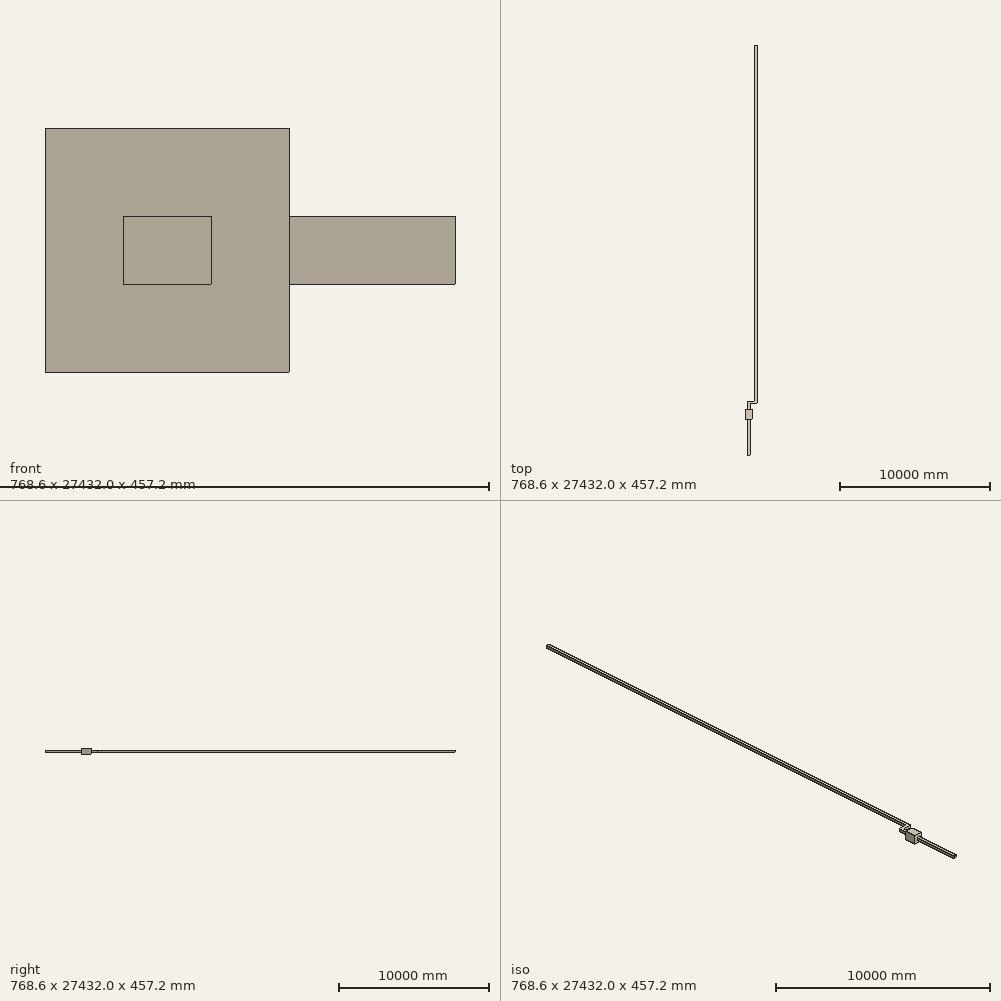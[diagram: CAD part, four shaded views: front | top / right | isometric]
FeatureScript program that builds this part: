
annotation { "Feature Type Name" : "Feature", "Feature Type Description" : "" }
export const myFeature = defineFeature(function(context is Context, id is Id, definition is map)
    precondition{}
    {
        {
            var Q0;
            Q0=qCreatedBy(makeId("Front.planeOp"),FACE);
            var sketch = newSketch(context, id + "F0", { "sketchPlane" : qUnion([Q0])});
            skLineSegment(sketch, "E0.bottom", {"start": v(0, 0) * mm, "end": v(165.6, 0) * mm});
            skLineSegment(sketch, "E0.top", {"start": v(0, 127) * mm, "end": v(165.6, 127) * mm});
            skLineSegment(sketch, "E0.left", {"start": v(0, 0) * mm, "end": v(0, 127) * mm});
            skLineSegment(sketch, "E0.right", {"start": v(165.6, 0) * mm, "end": v(165.6, 127) * mm});
            skSolve(sketch);
        }
        {
            var Q0;
            Q0=makeQuery(id+"F0.imprint","IMPRINT",FACE,{"disambiguationData":[TD([[makeQuery(id+"F0.imprint","IMPRINT",EDGE,{"derivedFrom":sQuery(id+"F0.wireOp",EDGE,"E0.bottom")}),1.0]])]});
            extrude(context, id + "F1", {"entities" : qUnion([Q0]), "oppositeDirection" : true, "depth" : 2438.4 * mm, "offsetDistance" : 25.4 * mm});
        }
        {
            var Q0;
            Q0=makeQuery(id+"F1.opExtrude","CAP_FACE",FACE,{"disambiguationData":[OSD([sQuery(id+"F0.wireOp",EDGE,"E0.bottom"),sQuery(id+"F0.wireOp",EDGE,"E0.top"),sQuery(id+"F0.wireOp",EDGE,"E0.left"),sQuery(id+"F0.wireOp",EDGE,"E0.right")])],"isStart":false});
            var sketch = newSketch(context, id + "F2", { "sketchPlane" : qUnion([Q0])});
            skLineSegment(sketch, "E1.bottom", {"start": v(145.8, -165.1) * mm, "end": v(-311.4, -165.1) * mm});
            skLineSegment(sketch, "E1.top", {"start": v(145.8, 292.1) * mm, "end": v(-311.4, 292.1) * mm});
            skLineSegment(sketch, "E1.left", {"start": v(145.8, -165.1) * mm, "end": v(145.8, 292.1) * mm});
            skLineSegment(sketch, "E1.right", {"start": v(-311.4, -165.1) * mm, "end": v(-311.4, 292.1) * mm});
            skPoint(sketch, "E1.middle", {"position": v(-82.8, 63.5) * mm});
            skPoint(sketch, "E1.middle.positionSnap0", {"position": v(-82.8, 127) * mm});
            skPoint(sketch, "E1.middle.positionSnap1", {"position": v(0, 63.5) * mm});
            skPoint(sketch, "E1.centerSnap0", {"position": v(-82.8, 127) * mm});
            skPoint(sketch, "E1.centerSnap1", {"position": v(0, 63.5) * mm});
            skSolve(sketch);
        }
        {
            var Q0;
            Q0=makeQuery(id+"F2.imprint","IMPRINT",FACE,{"disambiguationData":[TD([[makeQuery(id+"F2.imprint","IMPRINT",EDGE,{"derivedFrom":makeQuery(id+"F1.opExtrude","CAP_EDGE",EDGE,{"disambiguationData":[OSD([sQuery(id+"F0.wireOp",EDGE,"E0.bottom")])],"isStart":false})}),-1.0]])]});
            var Q1;
            Q1=makeQuery(id+"F2.imprint","IMPRINT",FACE,{"disambiguationData":[TD([[makeQuery(id+"F2.imprint","IMPRINT",EDGE,{"derivedFrom":sQuery(id+"F2.wireOp",EDGE,"E1.bottom")}),-1.0]])]});
            extrude(context, id + "F3", {"entities" : qUnion([Q0, Q1]), "depth" : 609.6 * mm, "offsetDistance" : 25.4 * mm});
        }
        {
            var Q0;
            Q0=makeQuery(id+"F3.opExtrude","CAP_FACE",FACE,{"disambiguationData":[OSD([sQuery(id+"F2.wireOp",EDGE,"E1.bottom"),sQuery(id+"F2.wireOp",EDGE,"E1.top"),sQuery(id+"F2.wireOp",EDGE,"E1.left"),sQuery(id+"F2.wireOp",EDGE,"E1.right")])],"isStart":false});
            var sketch = newSketch(context, id + "F4", { "sketchPlane" : qUnion([Q0])});
            skLineSegment(sketch, "E2.bottom", {"start": v(0, 0) * mm, "end": v(-165.6, 0) * mm});
            skLineSegment(sketch, "E2.top", {"start": v(0, 127) * mm, "end": v(-165.6, 127) * mm});
            skLineSegment(sketch, "E2.left", {"start": v(0, 0) * mm, "end": v(0, 127) * mm});
            skLineSegment(sketch, "E2.right", {"start": v(-165.6, 0) * mm, "end": v(-165.6, 127) * mm});
            skPoint(sketch, "E2.middle", {"position": v(-82.8, 63.5) * mm});
            skPoint(sketch, "E2.middle.positionSnap0", {"position": v(145.8, 63.5) * mm});
            skPoint(sketch, "E2.middle.positionSnap1", {"position": v(-82.8, 292.1) * mm});
            skPoint(sketch, "E2.centerSnap0", {"position": v(145.8, 63.5) * mm});
            skPoint(sketch, "E2.centerSnap1", {"position": v(-82.8, 292.1) * mm});
            skSolve(sketch);
        }
        {
            var Q0;
            Q0=makeQuery(id+"F4.imprint","IMPRINT",FACE,{"disambiguationData":[TD([[makeQuery(id+"F4.imprint","IMPRINT",EDGE,{"derivedFrom":sQuery(id+"F4.wireOp",EDGE,"E2.bottom")}),-1.0]])]});
            extrude(context, id + "F5", {"entities" : qUnion([Q0]), "depth" : 203.2 * mm, "offsetDistance" : 25.4 * mm});
        }
        {
            var Q0;
            Q0=makeQuery(id+"F5.opExtrude","CAP_FACE",FACE,{"disambiguationData":[OSD([sQuery(id+"F4.wireOp",EDGE,"E2.bottom"),sQuery(id+"F4.wireOp",EDGE,"E2.top"),sQuery(id+"F4.wireOp",EDGE,"E2.left"),sQuery(id+"F4.wireOp",EDGE,"E2.right")])],"isStart":false});
            extrude(context, id + "F6", {"entities" : qUnion([Q0]), "operationType" : NewBodyOperationType.ADD, "depth" : 387.6 * mm, "offsetDistance" : 25.4 * mm});
        }
        {
            var Q0;
            {var subQ0=sQuery(id+"F4.wireOp",EDGE,"E2.right");Q0=makeQuery(id+"F6.boolean.opBoolean","MERGE",FACE,{"derivedFrom":[makeQuery(id+"F5.opExtrude","SWEPT_FACE",FACE,{"disambiguationData":[OSD([subQ0])]}),makeQuery(id+"F6.opExtrude","SWEPT_FACE",FACE,{"disambiguationData":[OSD([subQ0])]})]});}
            var sketch = newSketch(context, id + "F7", { "sketchPlane" : qUnion([Q0])});
            skLineSegment(sketch, "E3.bottom", {"start": v(3638.8, 127) * mm, "end": v(3473.2, 127) * mm});
            skLineSegment(sketch, "E3.top", {"start": v(3638.8, 0) * mm, "end": v(3473.2, 0) * mm});
            skLineSegment(sketch, "E3.left", {"start": v(3638.8, 127) * mm, "end": v(3638.8, 0) * mm});
            skLineSegment(sketch, "E3.right", {"start": v(3473.2, 127) * mm, "end": v(3473.2, 0) * mm});
            skSolve(sketch);
        }
        {
            var Q0;
            Q0=makeQuery(id+"F7.imprint","IMPRINT",FACE,{"disambiguationData":[TD([[makeQuery(id+"F7.imprint","IMPRINT",EDGE,{"derivedFrom":sQuery(id+"F7.wireOp",EDGE,"E3.bottom")}),1.0]])]});
            extrude(context, id + "F8", {"entities" : qUnion([Q0]), "operationType" : NewBodyOperationType.ADD, "depth" : 457.2 * mm, "offsetDistance" : 25.4 * mm});
        }
        {
            var Q0;
            Q0=makeQuery(id+"F8.boolean.opBoolean","MERGE",FACE,{"derivedFrom":[makeQuery(id+"F6.opExtrude","CAP_FACE",FACE,{"disambiguationData":[OSD([sQuery(id+"F4.wireOp",EDGE,"E2.bottom"),sQuery(id+"F4.wireOp",EDGE,"E2.top"),sQuery(id+"F4.wireOp",EDGE,"E2.left"),sQuery(id+"F4.wireOp",EDGE,"E2.right")])],"isStart":false}),makeQuery(id+"F8.opExtrude","SWEPT_FACE",FACE,{"disambiguationData":[OSD([sQuery(id+"F7.wireOp",EDGE,"E3.left")])]})]});
            var sketch = newSketch(context, id + "F9", { "sketchPlane" : qUnion([Q0])});
            skLineSegment(sketch, "E4.bottom", {"start": v(-622.8, 0) * mm, "end": v(-457.2, 0) * mm});
            skLineSegment(sketch, "E4.top", {"start": v(-622.8, 127) * mm, "end": v(-457.2, 127) * mm});
            skLineSegment(sketch, "E4.left", {"start": v(-622.8, 0) * mm, "end": v(-622.8, 127) * mm});
            skLineSegment(sketch, "E4.right", {"start": v(-457.2, 0) * mm, "end": v(-457.2, 127) * mm});
            skSolve(sketch);
        }
        {
            var Q0;
            Q0=makeQuery(id+"F9.imprint","IMPRINT",FACE,{"disambiguationData":[TD([[makeQuery(id+"F9.imprint","IMPRINT",EDGE,{"derivedFrom":sQuery(id+"F9.wireOp",EDGE,"E4.bottom")}),-1.0]])]});
            extrude(context, id + "F10", {"entities" : qUnion([Q0]), "operationType" : NewBodyOperationType.ADD, "depth" : 222 * mm, "offsetDistance" : 25.4 * mm});
        }
        {
            var Q0;
            Q0=makeQuery(id+"F10.opExtrude","CAP_FACE",FACE,{"disambiguationData":[OSD([sQuery(id+"F9.wireOp",EDGE,"E4.bottom"),sQuery(id+"F9.wireOp",EDGE,"E4.top"),sQuery(id+"F9.wireOp",EDGE,"E4.left"),sQuery(id+"F9.wireOp",EDGE,"E4.right")])],"isStart":false});
            extrude(context, id + "F11", {"entities" : qUnion([Q0]), "operationType" : NewBodyOperationType.ADD, "depth" : 23571.2 * mm, "offsetDistance" : 25.4 * mm});
        }
    });
